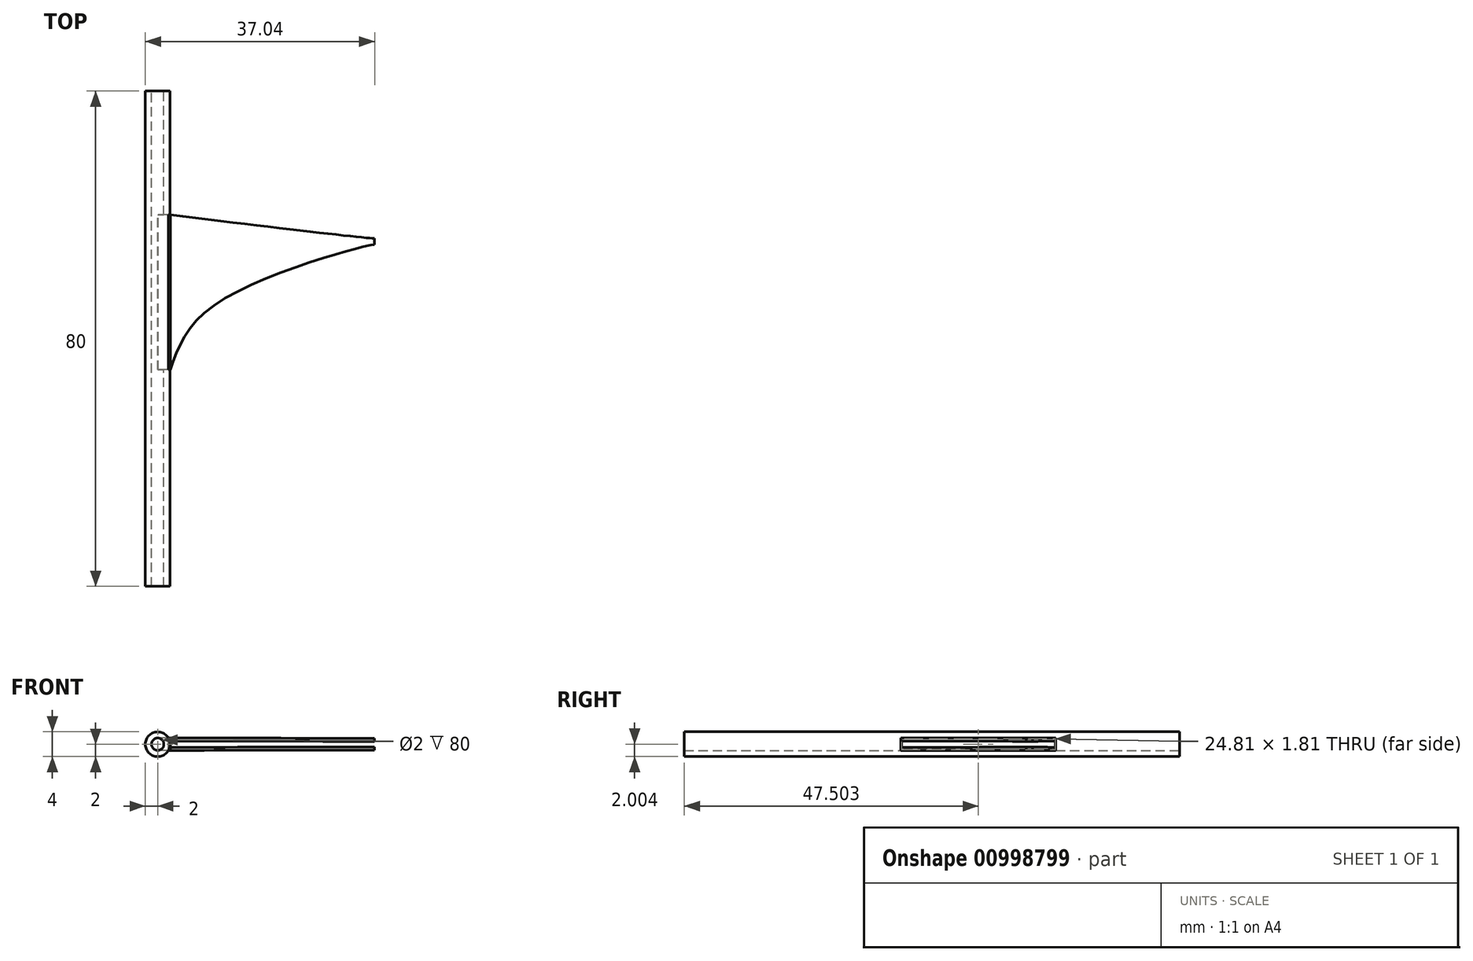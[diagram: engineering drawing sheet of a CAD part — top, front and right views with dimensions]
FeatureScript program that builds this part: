
annotation { "Feature Type Name" : "Feature", "Feature Type Description" : "" }
export const myFeature = defineFeature(function(context is Context, id is Id, definition is map)
    precondition{}
    {
        {
            var Q0;
            Q0=qCreatedBy(makeId("Front.planeOp"),FACE);
            var sketch = newSketch(context, id + "F0", { "sketchPlane" : qUnion([Q0])});
            skCircle(sketch, "E0", {"center": v(0, 0) * mm, "radius": 1 * mm});
            skCircle(sketch, "E1.0", {"center": v(0, 0) * mm, "radius": 2 * mm});
            skPoint(sketch, "E2", {"position": v(0, -1) * mm});
            skSolve(sketch);
        }
        {
            var Q0;
            Q0 = qSketchRegion(id + "F0", true);
            extrude(context, id + "F1", {"entities" : qUnion([Q0]), "depth" : 80 * mm, "offsetDistance" : 25 * mm});
        }
        {
            var Q0;
            Q0=sQuery(id+"F0.wireOp",VERTEX,"E2");
            var Q1;
            Q1=sQuery(id+"F0.wireOp",EDGE,"E0");
            cPlane(context, id + "F2", {"entities" : qUnion([Q0, Q1]), "cplaneType" : CPlaneType.LINE_POINT, "offset" : 25 * mm, "width" : 150 * mm, "height" : 150 * mm});
        }
        {
            var Q0;
            Q0=qCreatedBy(id+"F2.planeOp",FACE);
            cPlane(context, id + "F3", {"entities" : qUnion([Q0]), "cplaneType" : CPlaneType.OFFSET, "offset" : 45 * mm, "width" : 150 * mm, "height" : 150 * mm});
        }
        {
            var Q0;
            Q0=qCreatedBy(id+"F3.planeOp",FACE);
            var sketch = newSketch(context, id + "F4", { "sketchPlane" : qUnion([Q0])});
            skLineSegment(sketch, "E3", {"start": v(0, -1) * mm, "end": v(1, -1) * mm, "construction": true});
            skLineSegment(sketch, "E4", {"start": v(0, 1) * mm, "end": v(1, 1) * mm, "construction": true});
            skLineSegment(sketch, "E5", {"start": v(1, -1) * mm, "end": v(1, 1) * mm});
            skSolve(sketch);
        }
        {
            var Q0;
            Q0 = qSketchRegion(id + "F4", true);
            var Q1;
            Q1=sQuery(id+"F4.wireOp",EDGE,"E5");
            extrude(context, id + "F5", {"entities" : qUnion([Q0]), "bodyType" : ToolBodyType.SURFACE, "operationType" : NewBodyOperationType.REMOVE, "surfaceEntities" : qUnion([Q1]), "oppositeDirection" : true, "depth" : 25 * mm, "offsetDistance" : 25 * mm});
        }
        {
            var Q0;
            Q0=makeQuery(id+"F5.opExtrude","SWEPT_FACE",FACE,{"disambiguationData":[OSD([sQuery(id+"F4.wireOp",EDGE,"E5")])]});
            extrude(context, id + "F6", {"entities" : qUnion([Q0]), "operationType" : NewBodyOperationType.REMOVE, "oppositeDirection" : true, "depth" : 25 * mm, "offsetDistance" : 25 * mm, "hasSecondDirection" : true, "secondDirectionOppositeDirection" : false, "secondDirectionDepth" : 1 * mm});
        }
        {
            var Q0;
            Q0=makeQuery(id+"F6.boolean.opBoolean","INTERSECT",EDGE,{"derivedFrom":[makeQuery(id+"F1.opExtrude","SWEPT_FACE",FACE,{"disambiguationData":[OSD([sQuery(id+"F0.wireOp",EDGE,"E1.0")])]}),makeQuery(id+"F6.opExtrude","SWEPT_FACE",FACE,{"disambiguationData":[OSD([sQuery(id+"F4.wireOp",VERTEX,"E5.start")])]})]});
            var Q1;
            Q1=makeQuery(id+"F6.boolean.opBoolean","INTERSECT",EDGE,{"derivedFrom":[makeQuery(id+"F1.opExtrude","SWEPT_FACE",FACE,{"disambiguationData":[OSD([sQuery(id+"F0.wireOp",EDGE,"E1.0")])]}),makeQuery(id+"F6.opExtrude","SWEPT_FACE",FACE,{"disambiguationData":[OSD([sQuery(id+"F4.wireOp",VERTEX,"E5.end")])]})]});
            cPlane(context, id + "F7", {"entities" : qUnion([Q0, Q1]), "cplaneType" : CPlaneType.LINE_ANGLE, "offset" : 25 * mm, "angle" : 0 * degree, "width" : 150 * mm, "height" : 150 * mm});
        }
        {
            var Q0;
            Q0=qCreatedBy(id+"F7.planeOp",FACE);
            var sketch = newSketch(context, id + "F8", { "sketchPlane" : qUnion([Q0])});
            skLineSegment(sketch, "E6.bottom", {"start": v(-20, -1) * mm, "end": v(-45, -1) * mm});
            skLineSegment(sketch, "E6.top", {"start": v(-20, 1) * mm, "end": v(-45, 1) * mm});
            skLineSegment(sketch, "E6.left", {"start": v(-20, -1) * mm, "end": v(-20, 1) * mm});
            skLineSegment(sketch, "E6.right", {"start": v(-45, -1) * mm, "end": v(-45, 1) * mm});
            skLineSegment(sketch, "E7", {"start": v(-45, 0) * mm, "end": v(-20, 0) * mm});
            skSolve(sketch);
        }
        {
            var Q0;
            Q0 = qSketchRegion(id + "F8", true);
            extrude(context, id + "F9", {"entities" : qUnion([Q0]), "depth" : 0.3 * mm, "offsetDistance" : 25 * mm});
        }
        {
            var Q0;
            Q0=makeQuery(id+"F9.opExtrude","CAP_FACE",FACE,{"disambiguationData":[OSD([sQuery(id+"F8.wireOp",EDGE,"E6.bottom"),sQuery(id+"F8.wireOp",EDGE,"E6.top"),sQuery(id+"F8.wireOp",EDGE,"E6.left"),sQuery(id+"F8.wireOp",EDGE,"E6.right")])],"isStart":false});
            var Q1;
            Q1=makeQuery(id+"F9.opExtrude","CAP_FACE",FACE,{"disambiguationData":[OSD([sQuery(id+"F8.wireOp",EDGE,"E6.bottom"),sQuery(id+"F8.wireOp",EDGE,"E6.top"),sQuery(id+"F8.wireOp",EDGE,"E6.left"),sQuery(id+"F8.wireOp",EDGE,"E6.right")])],"isStart":true});
            var Q2;
            Q2=makeQuery(id+"F9.opExtrude","SWEPT_BODY",BODY,{"disambiguationData":[OSD([sQuery(id+"F8.wireOp",EDGE,"E6.bottom"),sQuery(id+"F8.wireOp",EDGE,"E6.top"),sQuery(id+"F8.wireOp",EDGE,"E6.left"),sQuery(id+"F8.wireOp",EDGE,"E6.right")])]});
            shell(context, id + "F10", {"entities" : qUnion([Q0, Q1]), "parts" : qUnion([Q2]), "thickness" : 0.1 * mm});
        }
        {
            var Q0;
            Q0=makeQuery(id+"F9.opExtrude","SWEPT_FACE",FACE,{"disambiguationData":[OSD([sQuery(id+"F8.wireOp",EDGE,"E6.bottom")])]});
            var sketch = newSketch(context, id + "F11", { "sketchPlane" : qUnion([Q0])});
            skFitSpline(sketch, "E8", {"points": [v(2.03, 45) * mm, v(8.82, 34.8) * mm, v(31.95, 25.48) * mm, v(34.98, 24.78) * mm], "startDerivative": vector(10.95, -31.1) * mm, "endDerivative": vector(12.07, -2.32) * mm});
            skFitSpline(sketch, "E9", {"points": [v(2.03, 20) * mm, v(35.03, 23.77) * mm, v(34.98, 23.74) * mm], "startDerivative": vector(51.53, 6.22) * mm, "endDerivative": vector(-2, -0.91) * mm});
            skLineSegment(sketch, "E10", {"start": v(34.98, 24.78) * mm, "end": v(35.03, 23.77) * mm});
            skSolve(sketch);
        }
        {
            var Q0;
            Q0=makeQuery(id+"F11.imprint","IMPRINT",FACE,{"disambiguationData":[TD([[makeQuery(id+"F11.imprint","IMPRINT",EDGE,{"derivedFrom":sQuery(id+"F11.wireOp",EDGE,"E8")}),-1.0]])]});
            extrude(context, id + "F12", {"entities" : qUnion([Q0]), "oppositeDirection" : true, "depth" : 0.5 * mm, "offsetDistance" : 25 * mm});
        }
        {
            var Q0;
            Q0=sQuery(id+"F8.wireOp",EDGE,"E7");
            cPlane(context, id + "F13", {"entities" : qUnion([Q0]), "cplaneType" : CPlaneType.LINE_ANGLE, "offset" : 25 * mm, "angle" : 0 * degree, "width" : 150 * mm, "height" : 150 * mm});
        }
        {
            var Q0;
            Q0=makeQuery(id+"F12.opExtrude","SWEPT_BODY",BODY,{"disambiguationData":[OSD([sQuery(id+"F8.wireOp",EDGE,"E6.bottom"),sQuery(id+"F11.wireOp",EDGE,"E8"),sQuery(id+"F11.wireOp",EDGE,"E9"),sQuery(id+"F11.wireOp",EDGE,"E10")])]});
            var Q1;
            Q1=qCreatedBy(id+"F13.planeOp",FACE);
            mirror(context, id + "F14", {"entities" : qUnion([Q0]), "mirrorPlane" : qUnion([Q1])});
        }
    });
